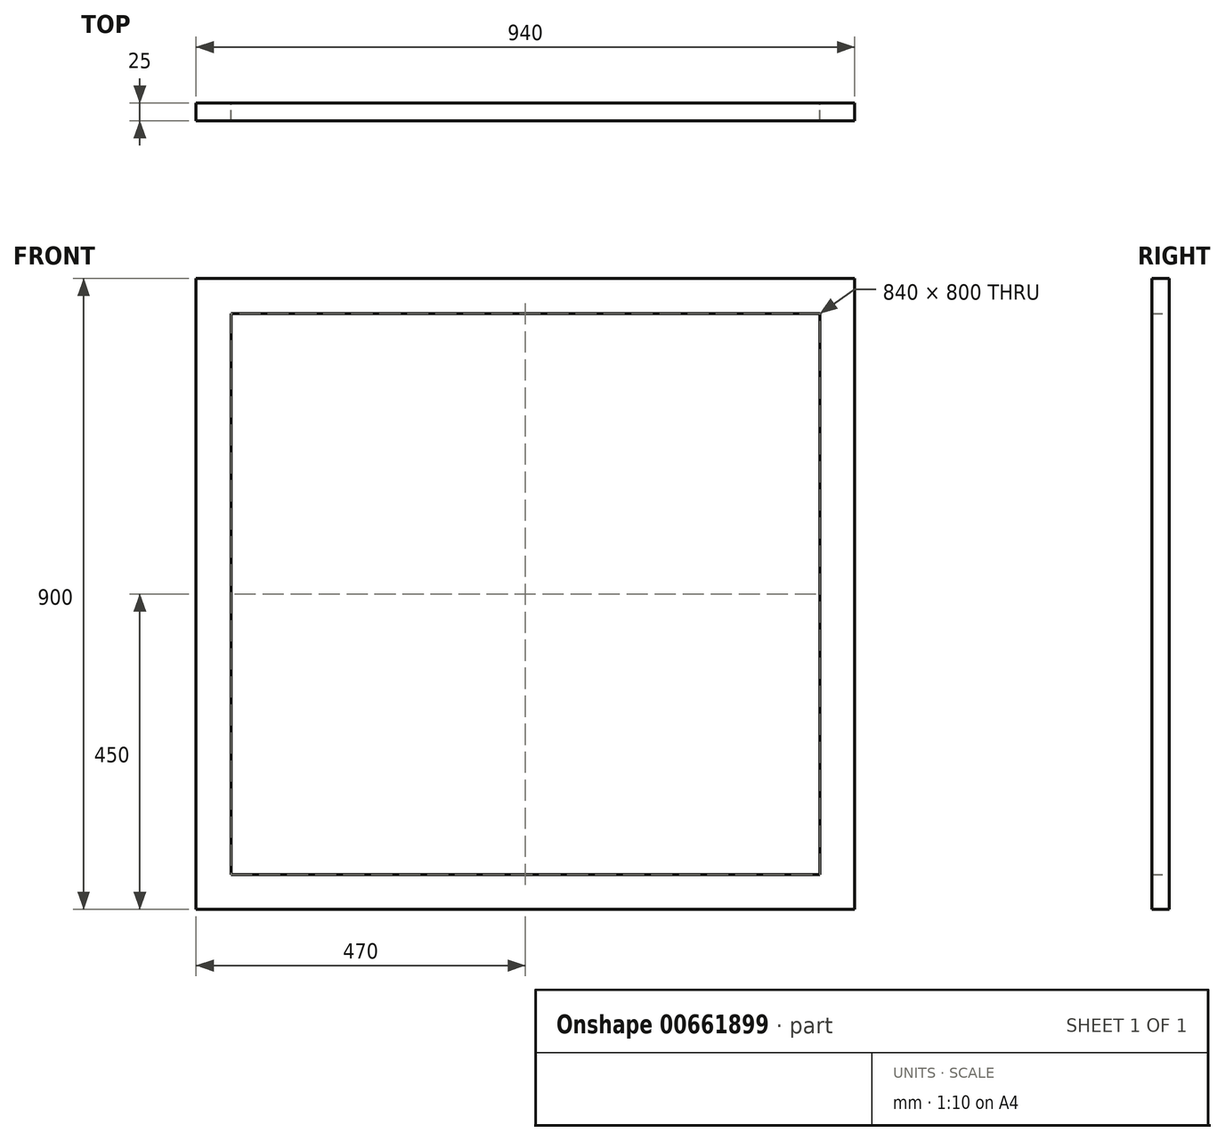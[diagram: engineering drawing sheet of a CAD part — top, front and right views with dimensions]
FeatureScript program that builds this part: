
annotation { "Feature Type Name" : "Feature", "Feature Type Description" : "" }
export const myFeature = defineFeature(function(context is Context, id is Id, definition is map)
    precondition{}
    {
        {
            var Q0;
            Q0=qCreatedBy(makeId("Front.planeOp"),FACE);
            var sketch = newSketch(context, id + "F0", { "sketchPlane" : qUnion([Q0])});
            skLineSegment(sketch, "E0.bottom", {"start": v(470, 450) * mm, "end": v(-470, 450) * mm});
            skLineSegment(sketch, "E0.top", {"start": v(470, -450) * mm, "end": v(-470, -450) * mm});
            skLineSegment(sketch, "E0.left", {"start": v(470, 450) * mm, "end": v(470, -450) * mm});
            skLineSegment(sketch, "E0.right", {"start": v(-470, 450) * mm, "end": v(-470, -450) * mm});
            skPoint(sketch, "E0.middle", {"position": v(0, 0) * mm});
            skLineSegment(sketch, "E1.bottom", {"start": v(420, 400) * mm, "end": v(-420, 400) * mm});
            skLineSegment(sketch, "E1.top", {"start": v(420, -400) * mm, "end": v(-420, -400) * mm});
            skLineSegment(sketch, "E1.left", {"start": v(420, 400) * mm, "end": v(420, -400) * mm});
            skLineSegment(sketch, "E1.right", {"start": v(-420, 400) * mm, "end": v(-420, -400) * mm});
            skSolve(sketch);
        }
        {
            var Q0;
            Q0=makeQuery(id+"F0.imprint","IMPRINT",FACE,{"disambiguationData":[TD([[makeQuery(id+"F0.imprint","IMPRINT",EDGE,{"derivedFrom":sQuery(id+"F0.wireOp",EDGE,"E1.bottom")}),1.0]])]});
            var sketch = newSketch(context, id + "F1", { "sketchPlane" : qUnion([Q0])});
            skSolve(sketch);
        }
        {
            var Q0;
            Q0=makeQuery(id+"F0.imprint","IMPRINT",FACE,{"disambiguationData":[TD([[makeQuery(id+"F0.imprint","IMPRINT",EDGE,{"derivedFrom":sQuery(id+"F0.wireOp",EDGE,"E0.bottom")}),1.0]])]});
            extrude(context, id + "F2", {"entities" : qUnion([Q0]), "depth" : 25 * mm, "offsetDistance" : 25 * mm});
        }
    });
